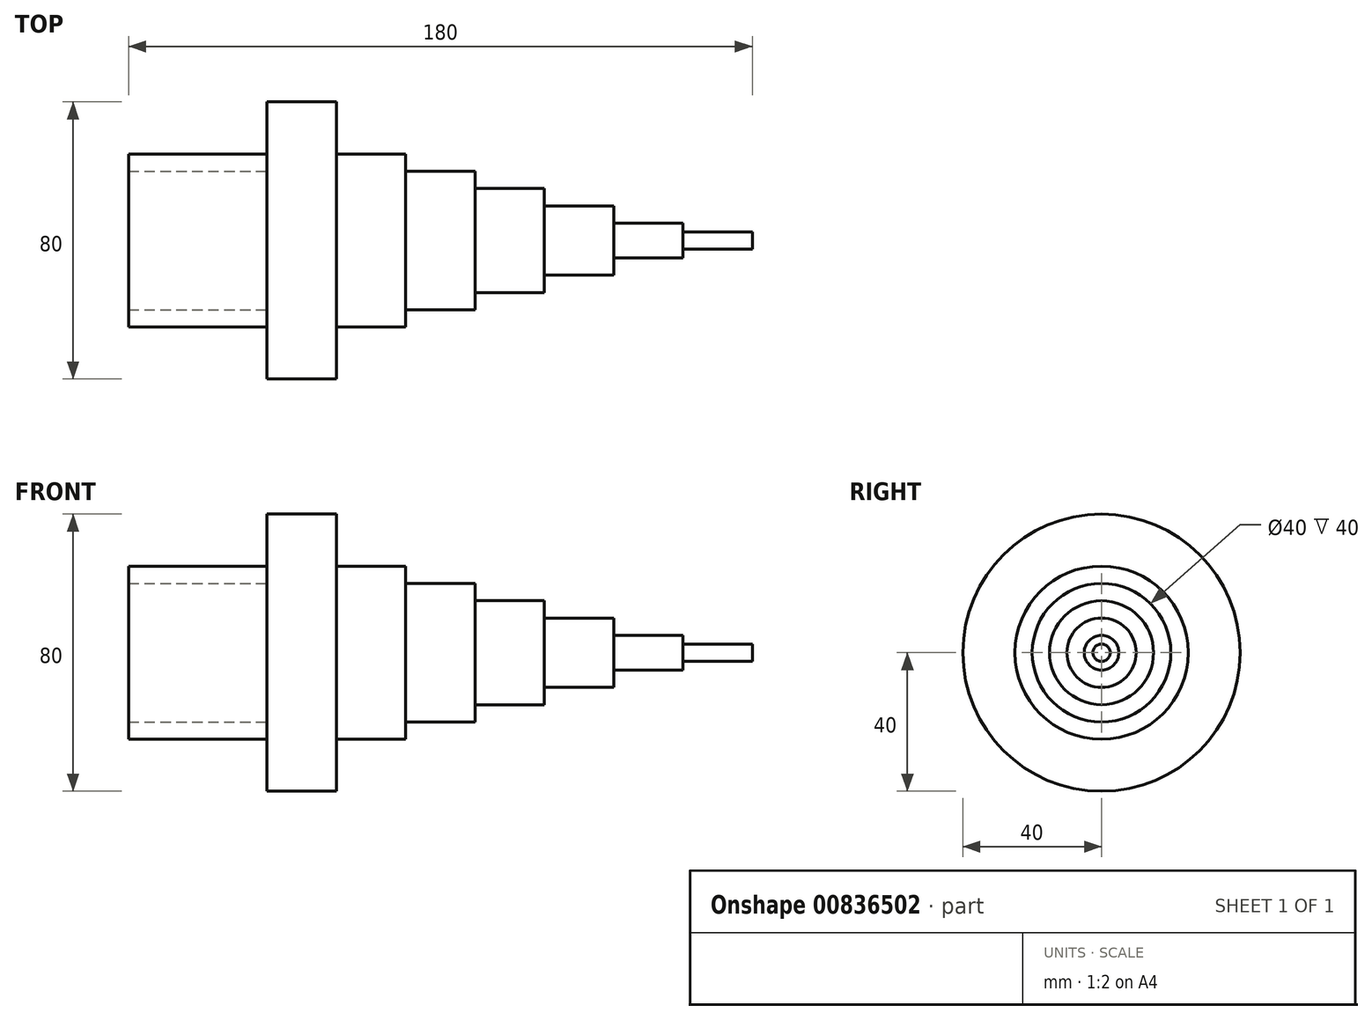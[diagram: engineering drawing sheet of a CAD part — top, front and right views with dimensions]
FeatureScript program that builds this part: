
annotation { "Feature Type Name" : "Feature", "Feature Type Description" : "" }
export const myFeature = defineFeature(function(context is Context, id is Id, definition is map)
    precondition{}
    {
        {
            var Q0;
            Q0=qCreatedBy(makeId("Top.planeOp"),FACE);
            var sketch = newSketch(context, id + "F0", { "sketchPlane" : qUnion([Q0])});
            skLineSegment(sketch, "E0", {"start": v(-61.57, 20) * mm, "end": v(-21.57, 20) * mm});
            skLineSegment(sketch, "E1", {"start": v(-61.57, 20) * mm, "end": v(-61.57, 25) * mm});
            skLineSegment(sketch, "E2", {"start": v(-61.57, 25) * mm, "end": v(-21.57, 25) * mm});
            skLineSegment(sketch, "E3", {"start": v(-21.57, 25) * mm, "end": v(-21.57, 40) * mm});
            skLineSegment(sketch, "E4", {"start": v(-21.57, 40) * mm, "end": v(-1.57, 40) * mm});
            skLineSegment(sketch, "E5", {"start": v(-1.57, 40) * mm, "end": v(-1.57, 25) * mm});
            skLineSegment(sketch, "E6", {"start": v(-1.57, 25) * mm, "end": v(18.43, 25) * mm});
            skLineSegment(sketch, "E7", {"start": v(18.43, 25) * mm, "end": v(18.43, 20) * mm});
            skLineSegment(sketch, "E8", {"start": v(18.43, 20) * mm, "end": v(38.43, 20) * mm});
            skLineSegment(sketch, "E9", {"start": v(38.43, 20) * mm, "end": v(38.43, 15) * mm});
            skLineSegment(sketch, "E10", {"start": v(38.43, 15) * mm, "end": v(58.43, 15) * mm});
            skLineSegment(sketch, "E11", {"start": v(58.43, 15) * mm, "end": v(58.43, 10) * mm});
            skLineSegment(sketch, "E12", {"start": v(58.43, 10) * mm, "end": v(78.43, 10) * mm});
            skLineSegment(sketch, "E13", {"start": v(78.43, 10) * mm, "end": v(78.43, 5) * mm});
            skLineSegment(sketch, "E14", {"start": v(78.43, 5) * mm, "end": v(98.43, 5) * mm});
            skLineSegment(sketch, "E15", {"start": v(98.43, 5) * mm, "end": v(98.43, 2.5) * mm});
            skLineSegment(sketch, "E16", {"start": v(98.43, 2.5) * mm, "end": v(118.43, 2.5) * mm});
            skLineSegment(sketch, "E17", {"start": v(118.43, 2.5) * mm, "end": v(118.43, 0) * mm});
            skLineSegment(sketch, "E18", {"start": v(118.43, 0) * mm, "end": v(-21.57, 0) * mm});
            skLineSegment(sketch, "E19", {"start": v(-21.57, 0) * mm, "end": v(-21.57, 20) * mm});
            skSolve(sketch);
        }
        {
            var Q0;
            Q0=makeQuery(id+"F0.imprint","IMPRINT",FACE,{"disambiguationData":[TD([[makeQuery(id+"F0.imprint","IMPRINT",EDGE,{"derivedFrom":sQuery(id+"F0.wireOp",EDGE,"E0")}),1.0]])]});
            var Q1;
            Q1=sQuery(id+"F0.wireOp",EDGE,"E18");
            revolve(context, id + "F1", {"surfaceOperationType" : NewSurfaceOperationType.NEW, "entities" : qUnion([Q0]), "axis" : qUnion([Q1]), "revolveType" : RevolveType.FULL});
        }
    });
